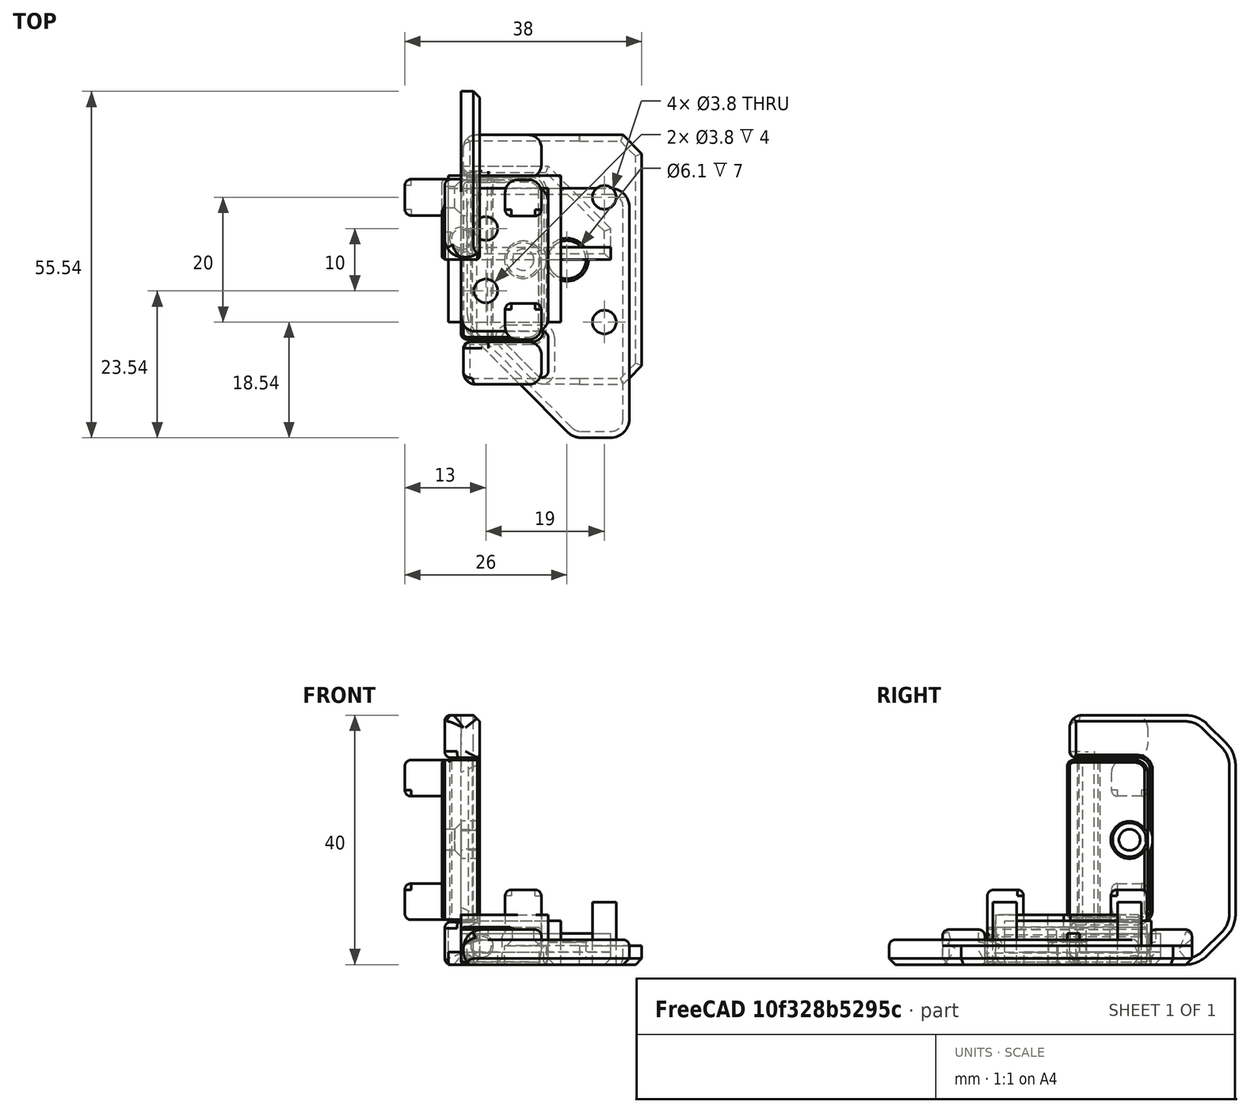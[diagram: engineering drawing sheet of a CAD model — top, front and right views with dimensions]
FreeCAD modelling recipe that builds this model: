
FCSTD DOCUMENT  (FreeCAD 0.19R24291 (Git))
Label: door-hingle
License: Other
LicenseURL: GPL3
objects: Part::Box×7, Part::Feature×5, Part::Chamfer×5, Part::MultiFuse×5, Part::Cylinder×4, Part::Cut×3, Part::Compound2×1, Part::Refine×1
note: 30 computed .brp shape members not serialized (recipe doc carries the construction recipe); baked Part::Feature solids carry a one-line shape summary decoded from their .brp

FEATURE [Part::Feature] Solid493
  shape: bbox 5.857 x 26.66 x 40.01 mm, 77 faces (baked)
FEATURE [Part::Feature] Solid494
  shape: bbox 12 x 12.9 x 25.6 mm, 62 faces (baked)
FEATURE [Part::Compound2] Compound037
  Links = -> [Solid493,Solid494]
  Placement = pos=(-5.1e-15,20,3) rot=(0.57735,0.57735,-0.57735;2.0944rad)
FEATURE [Part::Box] Box  label="Cube"
  AttacherType = Attacher::AttachEngine3D
  Height = 3
  Length = 10
  Placement = pos=(19,-20,0) rot=(0,0,1;0rad)
  Width = 40
FEATURE [Part::Cylinder] Cylinder
  Angle = 360
  AttacherType = Attacher::AttachEngine3D
  Height = 10
  Placement = pos=(23,10,0) rot=(0,0,1;0rad)
  Radius = 1.9
FEATURE [Part::Chamfer] Chamfer
  Base = -> Box
  Edges = 2 edges r=3: [Edge5,Edge7]
FEATURE [Part::Chamfer] Chamfer001
  Base = -> Chamfer
  Edges = 5 edges r=1: [Edge3,Edge10,Edge12,Edge14,Edge16]
FEATURE [Part::MultiFuse] Fusion
  Shapes = -> [Compound037,Chamfer001]
FEATURE [Part::Cylinder] Cylinder001
  Angle = 360
  AttacherType = Attacher::AttachEngine3D
  Height = 10
  Placement = pos=(23,-10,0) rot=(0,0,1;0rad)
  Radius = 1.9
FEATURE [Part::MultiFuse] Fusion001
  Shapes = -> [Cylinder,Cylinder001]
FEATURE [Part::Feature] Fusion001001
  shape: bbox 3.8 x 23.8 x 10 mm, 6 faces, 2 solids (baked)
FEATURE [Part::Cut] Cut
  Base = -> Fusion
  Tool = -> Fusion001
FEATURE [Part::Feature] Solid495
  Placement = pos=(-68,-128.535,3) rot=(0,1,0;1.5708rad)
  shape: bbox 27.66 x 40.66 x 8.001 mm, 57 faces (baked)
FEATURE [Part::Cylinder] Cylinder002
  Angle = 360
  AttacherType = Attacher::AttachEngine3D
  Height = 10
  Placement = pos=(4,5,4) rot=(0,0,1;0rad)
  Radius = 1.9
FEATURE [Part::Box] Box001  label="Cube001"
  AttacherType = Attacher::AttachEngine3D
  Height = 7
  Length = 2
  Placement = pos=(14,-10,0) rot=(0,0,1;0rad)
  Width = 23
FEATURE [Part::Box] Box002  label="Cube002"
  AttacherType = Attacher::AttachEngine3D
  Height = 7
  Length = 18
  Placement = pos=(-2,11.47,0) rot=(0,0,1;0rad)
  Width = 2
FEATURE [Part::Box] Box003  label="Cube003"
  AttacherType = Attacher::AttachEngine3D
  Height = 2
  Length = 16
  Placement = pos=(-2,-10,0) rot=(0,0,1;0rad)
  Width = 23
FEATURE [Part::Cylinder] Cylinder003
  Angle = 360
  AttacherType = Attacher::AttachEngine3D
  Height = 10
  Placement = pos=(4,-5,4) rot=(0,0,1;0rad)
  Radius = 1.9
FEATURE [Part::MultiFuse] Fusion001002002
  Shapes = -> [Cylinder002,Cylinder003]
FEATURE [Part::Feature] Fusion001002002001
  Placement = pos=(0,0,-6) rot=(0,0,1;0rad)
  shape: bbox 3.8 x 13.8 x 10 mm, 6 faces, 2 solids (baked)
FEATURE [Part::Cut] Cut003
  Base = -> Solid495
  Tool = -> Fusion001002002
FEATURE [Part::MultiFuse] Fusion001002002002
  Shapes = -> [Box002,Box003,Box001]
FEATURE [Part::Cut] Cut004
  Base = -> Fusion001002002002
  Tool = -> Fusion001002002001
FEATURE [Part::Box] Box004  label="Cube004"
  AttacherType = Attacher::AttachEngine3D
  Height = 2
  Length = 24
  Width = 15
FEATURE [Part::Box] Box005  label="Cube005"
  AttacherType = Attacher::AttachEngine3D
  Height = 5
  Length = 2
  Width = 15
FEATURE [Part::Box] Box006  label="Cube006"
  AttacherType = Attacher::AttachEngine3D
  Height = 5
  Length = 24
  Width = 2
FEATURE [Part::Chamfer] Chamfer002
  Base = -> Box004
  Edges = 1 edges r=10: [Edge7]
FEATURE [Part::MultiFuse] Fusion001002002003
  Shapes = -> [Box006,Box005,Chamfer002]
FEATURE [Part::Refine] Fusion001002002003001
  Source = -> Fusion001002002003
FEATURE [Part::Chamfer] Chamfer003
  Base = -> Fusion001002002003001
  Edges = 1 edges r=1: [Edge1]
FEATURE [Part::Chamfer] Chamfer004
  Base = -> Chamfer003
  Edges = 6 edges r=1: [Edge3,Edge11,Edge16,Edge17,Edge18,Edge19]
